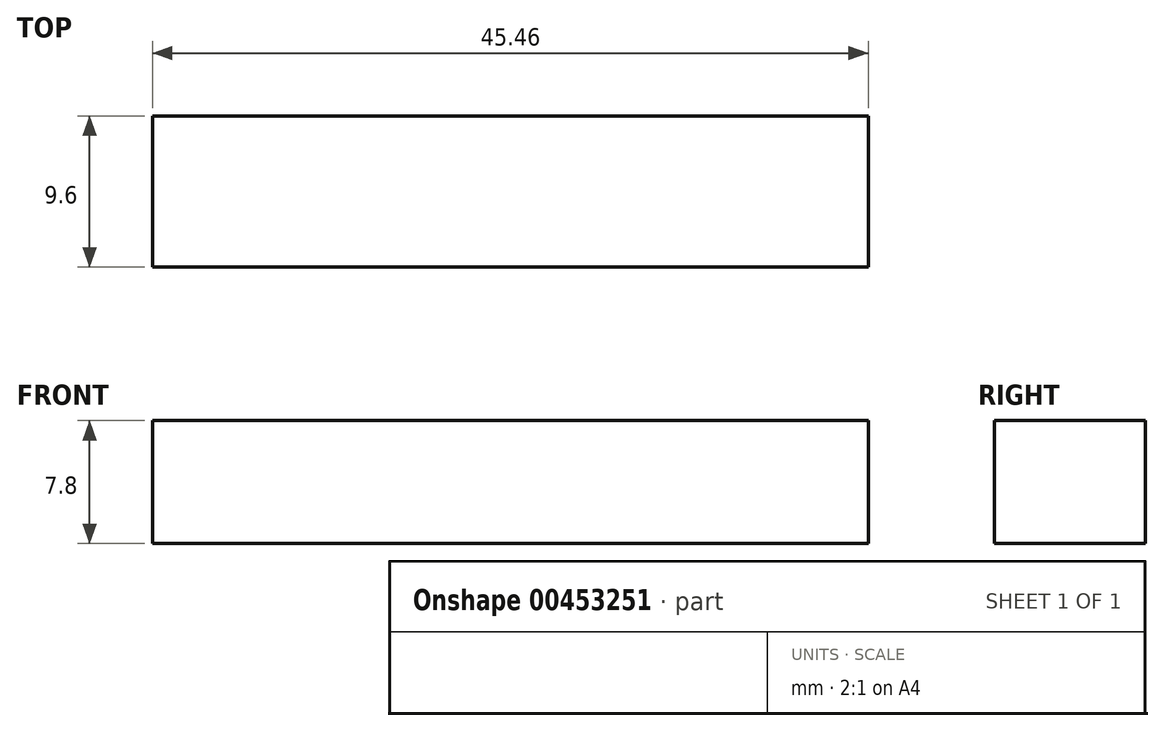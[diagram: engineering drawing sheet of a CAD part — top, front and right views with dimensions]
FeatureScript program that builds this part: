
annotation { "Feature Type Name" : "Feature", "Feature Type Description" : "" }
export const myFeature = defineFeature(function(context is Context, id is Id, definition is map)
    precondition{}
    {
        {
            var Q0;
            Q0=qCreatedBy(makeId("Front.planeOp"),FACE);
            var sketch = newSketch(context, id + "F0", { "sketchPlane" : qUnion([Q0])});
            skLineSegment(sketch, "E0.bottom", {"start": v(-33.24, 9.48) * mm, "end": v(12.22, 9.48) * mm});
            skLineSegment(sketch, "E0.top", {"start": v(-33.24, 1.68) * mm, "end": v(12.22, 1.68) * mm});
            skLineSegment(sketch, "E0.left", {"start": v(-33.24, 9.48) * mm, "end": v(-33.24, 1.68) * mm});
            skLineSegment(sketch, "E0.right", {"start": v(12.22, 9.48) * mm, "end": v(12.22, 1.68) * mm});
            skSolve(sketch);
        }
        {
            var Q0;
            Q0 = qSketchRegion(id + "F0", true);
            extrude(context, id + "F1", {"entities" : qUnion([Q0]), "depth" : 9.6 * mm});
        }
    });
